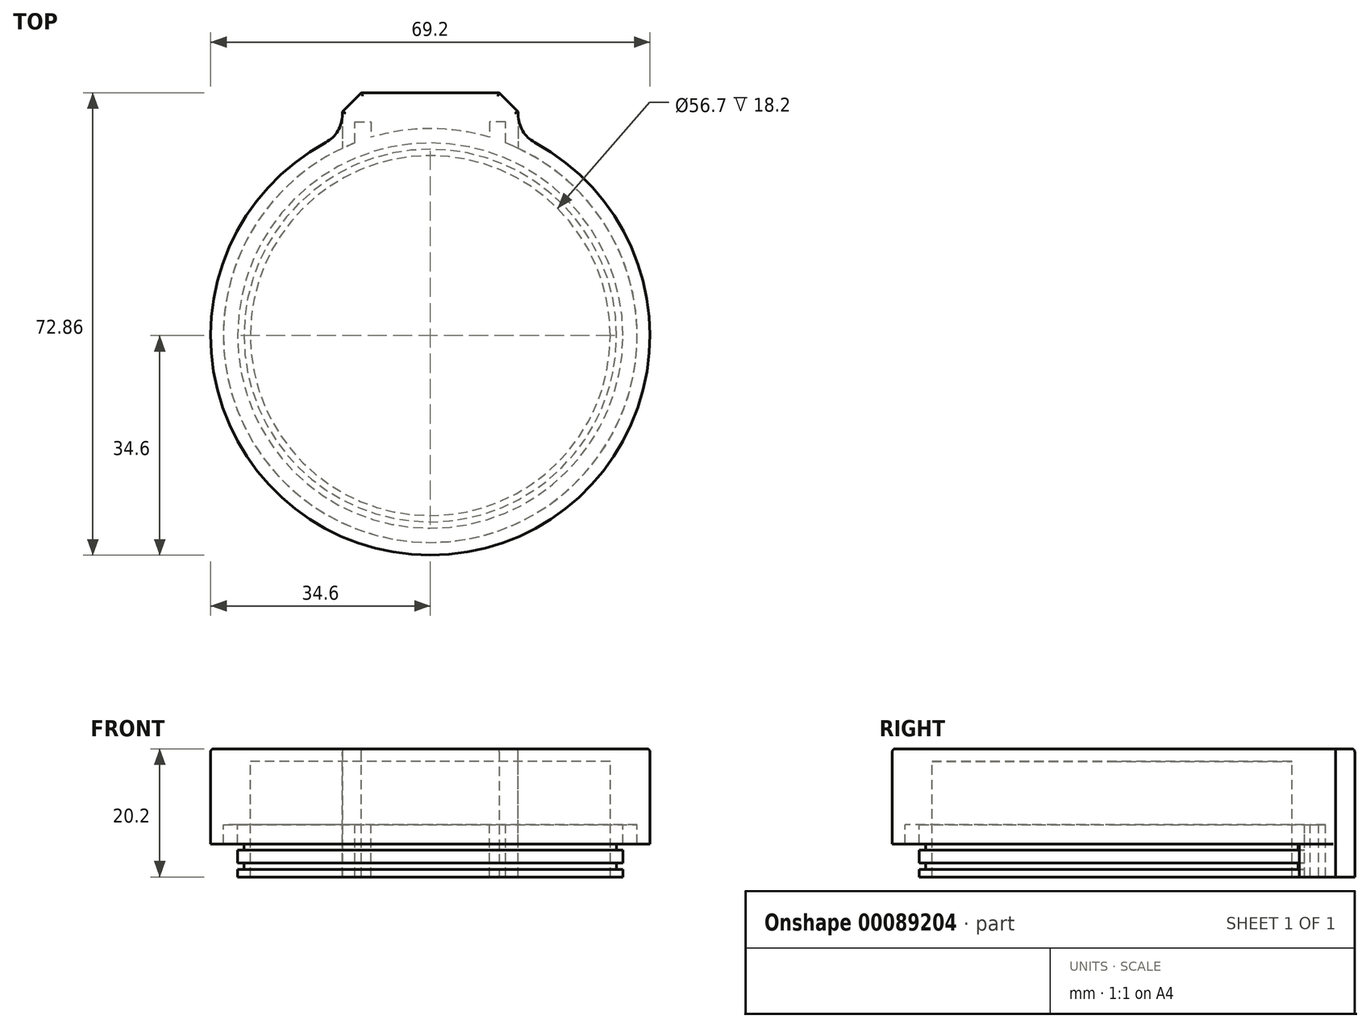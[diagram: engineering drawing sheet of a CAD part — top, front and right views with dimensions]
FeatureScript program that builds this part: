
annotation { "Feature Type Name" : "Feature", "Feature Type Description" : "" }
export const myFeature = defineFeature(function(context is Context, id is Id, definition is map)
    precondition{}
    {
        {
            var Q0;
            Q0=qCreatedBy(makeId("Front.planeOp"),FACE);
            var sketch = newSketch(context, id + "F0", { "sketchPlane" : qUnion([Q0])});
            skLineSegment(sketch, "E0", {"start": v(-30.35, 0) * mm, "end": v(-30.35, 1.2) * mm});
            skLineSegment(sketch, "E1", {"start": v(-30.35, 20.2) * mm, "end": v(0, 20.2) * mm});
            skLineSegment(sketch, "E2", {"start": v(0, 20.2) * mm, "end": v(0, 18.2) * mm});
            skLineSegment(sketch, "E3", {"start": v(0, 18.2) * mm, "end": v(-28.35, 18.2) * mm});
            skLineSegment(sketch, "E4", {"start": v(-30.35, 0) * mm, "end": v(-28.35, 0) * mm});
            skLineSegment(sketch, "E5", {"start": v(-28.35, 0) * mm, "end": v(-28.35, 18.2) * mm});
            skLineSegment(sketch, "E6", {"start": v(-30.35, 2.2) * mm, "end": v(-29.35, 2.2) * mm});
            skLineSegment(sketch, "E7", {"start": v(-29.35, 2.2) * mm, "end": v(-29.35, 1.2) * mm});
            skLineSegment(sketch, "E8", {"start": v(-29.35, 1.2) * mm, "end": v(-30.35, 1.2) * mm});
            skLineSegment(sketch, "E9", {"start": v(-30.35, 5.2) * mm, "end": v(-29.35, 5.2) * mm});
            skLineSegment(sketch, "E10", {"start": v(-29.35, 5.2) * mm, "end": v(-29.35, 4.2) * mm});
            skLineSegment(sketch, "E11", {"start": v(-29.35, 4.2) * mm, "end": v(-30.35, 4.2) * mm});
            skLineSegment(sketch, "E12.trimOffspring", {"start": v(-30.35, 5.2) * mm, "end": v(-30.35, 8.2) * mm});
            skLineSegment(sketch, "E13.trimOffspring", {"start": v(-30.35, 2.2) * mm, "end": v(-30.35, 4.2) * mm});
            skPoint(sketch, "E14.end.orphan", {"position": v(-26, 20.2) * mm});
            skLineSegment(sketch, "E15", {"start": v(-30.35, 20.2) * mm, "end": v(-32.6, 20.2) * mm});
            skPoint(sketch, "E16.end.orphan", {"position": v(-32.55, 18.2) * mm});
            skLineSegment(sketch, "E17", {"start": v(-32.6, 20.2) * mm, "end": v(-32.6, 8.2) * mm});
            skLineSegment(sketch, "E18", {"start": v(-32.6, 8.2) * mm, "end": v(-30.35, 8.2) * mm});
            skPoint(sketch, "E19.orphan", {"position": v(-30.35, 18.2) * mm});
            skSolve(sketch);
        }
        {
            var Q0;
            Q0 = qSketchRegion(id + "F0", true);
            var Q1;
            Q1=sQuery(id+"F0.wireOp",EDGE,"E2");
            revolve(context, id + "F1", {"entities" : qUnion([Q0]), "axis" : qUnion([Q1]), "revolveType" : RevolveType.FULL});
        }
        {
            var Q0;
            Q0=makeQuery(id+"F1.opRevolve","SWEPT_FACE",FACE,{"disambiguationData":[OSD([sQuery(id+"F0.wireOp",EDGE,"E1")])]});
            var sketch = newSketch(context, id + "F2", { "sketchPlane" : qUnion([Q0])});
            skArc(sketch, "E20", {"start": v(-11.85, 30.37) * mm, "mid": v(0, -32.6) * mm, "end": v(11.85, 30.37) * mm});
            skArc(sketch, "E21", {"start": v(-13.85, 31.7) * mm, "mid": v(0, -34.6) * mm, "end": v(13.85, 31.7) * mm});
            skLineSegment(sketch, "E22", {"start": v(-11.85, 30.37) * mm, "end": v(-11.85, 33.67) * mm});
            skLineSegment(sketch, "E23", {"start": v(-11.85, 33.67) * mm, "end": v(-9.35, 33.67) * mm});
            skLineSegment(sketch, "E24", {"start": v(-9.35, 33.67) * mm, "end": v(-9.35, 31.23) * mm});
            skLineSegment(sketch, "E25.MirrorCS", {"start": v(11.85, 33.67) * mm, "end": v(9.35, 33.67) * mm});
            skLineSegment(sketch, "E26.MirrorCS", {"start": v(9.35, 33.67) * mm, "end": v(9.35, 31.23) * mm});
            skLineSegment(sketch, "E27.MirrorCS", {"start": v(11.85, 30.37) * mm, "end": v(11.85, 33.67) * mm});
            skArc(sketch, "E28.trimOffspring", {"start": v(9.35, 31.23) * mm, "mid": v(0, 32.6) * mm, "end": v(-9.35, 31.23) * mm, "construction": true});
            skLineSegment(sketch, "E29", {"start": v(-13.85, 31.7) * mm, "end": v(-13.85, 38.26) * mm});
            skLineSegment(sketch, "E30", {"start": v(-13.85, 38.26) * mm, "end": v(13.85, 38.26) * mm});
            skLineSegment(sketch, "E31", {"start": v(13.85, 38.26) * mm, "end": v(13.85, 31.7) * mm});
            skArc(sketch, "E32.trimOffspring", {"start": v(9.35, 31.23) * mm, "mid": v(0, 32.6) * mm, "end": v(-9.35, 31.23) * mm});
            skSolve(sketch);
        }
        {
            var Q0;
            Q0 = qSketchRegion(id + "F2", true);
            extrude(context, id + "F3", {"entities" : qUnion([Q0]), "operationType" : NewBodyOperationType.ADD, "oppositeDirection" : true, "depth" : 15 * mm});
        }
        {
            var Q0;
            Q0=makeQuery(id+"F1.opRevolve","SWEPT_FACE",FACE,{"disambiguationData":[OSD([sQuery(id+"F0.wireOp",EDGE,"E18")])]});
            var sketch = newSketch(context, id + "F4", { "sketchPlane" : qUnion([Q0])});
            skArc(sketch, "E33.0", {"start": v(-13.85, -31.7) * mm, "mid": v(0, 34.6) * mm, "end": v(13.85, -31.7) * mm});
            skLineSegment(sketch, "E33.1", {"start": v(-13.85, -31.7) * mm, "end": v(-13.85, -38.26) * mm});
            skLineSegment(sketch, "E33.2", {"start": v(-13.85, -38.26) * mm, "end": v(13.85, -38.26) * mm});
            skLineSegment(sketch, "E33.3", {"start": v(13.85, -38.26) * mm, "end": v(13.85, -31.7) * mm});
            skCircle(sketch, "E33.4", {"center": v(0, 0) * mm, "radius": 30.35 * mm});
            skSolve(sketch);
        }
        {
            var Q0;
            Q0 = qSketchRegion(id + "F4", true);
            extrude(context, id + "F5", {"entities" : qUnion([Q0]), "operationType" : NewBodyOperationType.ADD, "oppositeDirection" : true, "depth" : 12 * mm});
        }
        {
            var Q0;
            Q0=makeQuery(id+"F1.opRevolve","SWEPT_FACE",FACE,{"disambiguationData":[OSD([sQuery(id+"F0.wireOp",EDGE,"E3")])]});
            var sketch = newSketch(context, id + "F6", { "sketchPlane" : qUnion([Q0])});
            skSolve(sketch);
        }
        {
            var Q0;
            Q0=makeQuery(id+"F3.opExtrude","CAP_FACE",FACE,{"disambiguationData":[OSD([sQuery(id+"F2.wireOp",EDGE,"E21"),sQuery(id+"F2.wireOp",EDGE,"E22"),sQuery(id+"F2.wireOp",EDGE,"E23"),sQuery(id+"F2.wireOp",EDGE,"E24"),sQuery(id+"F2.wireOp",EDGE,"E25.MirrorCS"),sQuery(id+"F2.wireOp",EDGE,"E26.MirrorCS"),sQuery(id+"F2.wireOp",EDGE,"E27.MirrorCS"),sQuery(id+"F2.wireOp",EDGE,"E29"),sQuery(id+"F2.wireOp",EDGE,"E30"),sQuery(id+"F2.wireOp",EDGE,"E31"),sQuery(id+"F2.wireOp",EDGE,"E20"),sQuery(id+"F2.wireOp",EDGE,"E32.trimOffspring")])],"isStart":false});
            var sketch = newSketch(context, id + "F7", { "sketchPlane" : qUnion([Q0])});
            skLineSegment(sketch, "E34", {"start": v(-13.85, -38.26) * mm, "end": v(13.85, -38.26) * mm});
            skLineSegment(sketch, "E35", {"start": v(13.85, -38.26) * mm, "end": v(13.85, -29.51) * mm});
            skLineSegment(sketch, "E36", {"start": v(-13.85, -38.26) * mm, "end": v(-13.85, -29.51) * mm});
            skArc(sketch, "E37.0", {"start": v(-11.85, -30.37) * mm, "mid": v(-12.86, -29.96) * mm, "end": v(-13.85, -29.51) * mm});
            skLineSegment(sketch, "E37.1", {"start": v(-11.85, -30.37) * mm, "end": v(-11.85, -33.67) * mm});
            skLineSegment(sketch, "E37.2", {"start": v(-11.85, -33.67) * mm, "end": v(-9.35, -33.67) * mm});
            skLineSegment(sketch, "E37.3", {"start": v(-9.35, -33.67) * mm, "end": v(-9.35, -31.23) * mm});
            skArc(sketch, "E37.4", {"start": v(9.35, -31.23) * mm, "mid": v(0, -32.6) * mm, "end": v(-9.35, -31.23) * mm});
            skLineSegment(sketch, "E37.5", {"start": v(9.35, -33.67) * mm, "end": v(9.35, -31.23) * mm});
            skLineSegment(sketch, "E37.6", {"start": v(11.85, -33.67) * mm, "end": v(9.35, -33.67) * mm});
            skLineSegment(sketch, "E37.7", {"start": v(11.85, -30.37) * mm, "end": v(11.85, -33.67) * mm});
            skArc(sketch, "E38.trimOffspring", {"start": v(13.85, -29.51) * mm, "mid": v(12.86, -29.96) * mm, "end": v(11.85, -30.37) * mm});
            skSolve(sketch);
        }
        {
            var Q0;
            Q0 = qSketchRegion(id + "F7", true);
            var Q1;
            Q1=makeQuery(id+"F1.opRevolve","SWEPT_FACE",FACE,{"disambiguationData":[OSD([sQuery(id+"F0.wireOp",EDGE,"E4")])]});
            extrude(context, id + "F8", {"entities" : qUnion([Q0]), "operationType" : NewBodyOperationType.ADD, "endBound" : BoundingType.UP_TO_SURFACE, "endBoundEntityFace" : qUnion([Q1]), "depth" : 25 * mm});
        }
        {
            var Q0;
            Q0=makeQuery(id+"F3.opExtrude","SWEPT_EDGE",EDGE,{"disambiguationData":[OSD([sQuery(id+"F2.wireOp",EDGE,"E21"),sQuery(id+"F2.wireOp",EDGE,"E29")])]});
            var Q1;
            Q1=makeQuery(id+"F3.opExtrude","SWEPT_EDGE",EDGE,{"disambiguationData":[OSD([sQuery(id+"F2.wireOp",EDGE,"E21"),sQuery(id+"F2.wireOp",EDGE,"E31")])]});
            var Q2;
            Q2=makeQuery(id+"F8.opExtrude","CAP_EDGE",EDGE,{"disambiguationData":[OSD([sQuery(id+"F7.wireOp",EDGE,"E36")])],"isStart":true});
            var Q3;
            Q3=makeQuery(id+"F8.opExtrude","CAP_EDGE",EDGE,{"disambiguationData":[OSD([sQuery(id+"F7.wireOp",EDGE,"E35")])],"isStart":true});
            fillet(context, id + "F9", {"entities" : qUnion([Q0, Q1, Q2, Q3]), "radius" : 5 * mm, "tangentPropagation" : true, "allowEdgeOverflow" : false});
        }
        {
            var Q0;
            Q0=makeQuery(id+"F8.boolean.opBoolean","MERGE",EDGE,{"derivedFrom":[makeQuery(id+"F3.opExtrude","SWEPT_EDGE",EDGE,{"disambiguationData":[OSD([sQuery(id+"F2.wireOp",EDGE,"E30"),sQuery(id+"F2.wireOp",EDGE,"E31")])]}),makeQuery(id+"F8.opExtrude","SWEPT_EDGE",EDGE,{"disambiguationData":[OSD([sQuery(id+"F7.wireOp",EDGE,"E34"),sQuery(id+"F7.wireOp",EDGE,"E35")])]})]});
            var Q1;
            Q1=makeQuery(id+"F8.boolean.opBoolean","MERGE",EDGE,{"derivedFrom":[makeQuery(id+"F3.opExtrude","SWEPT_EDGE",EDGE,{"disambiguationData":[OSD([sQuery(id+"F2.wireOp",EDGE,"E29"),sQuery(id+"F2.wireOp",EDGE,"E30")])]}),makeQuery(id+"F8.opExtrude","SWEPT_EDGE",EDGE,{"disambiguationData":[OSD([sQuery(id+"F7.wireOp",EDGE,"E34"),sQuery(id+"F7.wireOp",EDGE,"E36")])]})]});
            chamfer(context, id + "F10", {"entities" : qUnion([Q0, Q1]), "width" : 3 * mm, "tangentPropagation" : true});
        }
        {
            var Q0;
            Q0=makeQuery(id+"F3.opExtrude","CAP_EDGE",EDGE,{"disambiguationData":[OSD([sQuery(id+"F2.wireOp",EDGE,"E30")])],"isStart":true});
            var Q1;
            {var subQ0=sQuery(id+"F2.wireOp",EDGE,"E30");var subQ1=sQuery(id+"F2.wireOp",EDGE,"E29");Q1=makeQuery(id+"F10.opChamfer","BLEND_EDGE",EDGE,{"blendedFrom":[makeQuery(id+"F8.boolean.opBoolean","MERGE",EDGE,{"derivedFrom":[makeQuery(id+"F3.opExtrude","SWEPT_EDGE",EDGE,{"disambiguationData":[OSD([subQ1,subQ0])]}),makeQuery(id+"F8.opExtrude","SWEPT_EDGE",EDGE,{"disambiguationData":[OSD([sQuery(id+"F7.wireOp",EDGE,"E34"),sQuery(id+"F7.wireOp",EDGE,"E36")])]})]}),makeQuery(id+"F5.boolean.opBoolean","MERGE",FACE,{"derivedFrom":[makeQuery(id+"F3.boolean.opBoolean","MERGE",FACE,{"derivedFrom":[makeQuery(id+"F1.opRevolve","SWEPT_FACE",FACE,{"disambiguationData":[OSD([sQuery(id+"F0.wireOp",EDGE,"E1"),sQuery(id+"F0.wireOp",EDGE,"E15")])]}),makeQuery(id+"F3.opExtrude","CAP_FACE",FACE,{"disambiguationData":[OSD([sQuery(id+"F2.wireOp",EDGE,"E21"),sQuery(id+"F2.wireOp",EDGE,"E22"),sQuery(id+"F2.wireOp",EDGE,"E23"),sQuery(id+"F2.wireOp",EDGE,"E24"),sQuery(id+"F2.wireOp",EDGE,"E25.MirrorCS"),sQuery(id+"F2.wireOp",EDGE,"E26.MirrorCS"),sQuery(id+"F2.wireOp",EDGE,"E27.MirrorCS"),subQ1,subQ0,sQuery(id+"F2.wireOp",EDGE,"E31"),sQuery(id+"F2.wireOp",EDGE,"E20"),sQuery(id+"F2.wireOp",EDGE,"E32.trimOffspring")])],"isStart":true})]}),makeQuery(id+"F5.opExtrude","CAP_FACE",FACE,{"disambiguationData":[OSD([sQuery(id+"F4.wireOp",EDGE,"E33.0"),sQuery(id+"F4.wireOp",EDGE,"E33.1"),sQuery(id+"F4.wireOp",EDGE,"E33.2"),sQuery(id+"F4.wireOp",EDGE,"E33.3"),sQuery(id+"F4.wireOp",EDGE,"E33.4")])],"isStart":false})]})],"blendedInto":[makeQuery(id+"F5.boolean.opBoolean","MERGE",FACE,{"derivedFrom":[makeQuery(id+"F3.boolean.opBoolean","MERGE",FACE,{"derivedFrom":[makeQuery(id+"F1.opRevolve","SWEPT_FACE",FACE,{"disambiguationData":[OSD([sQuery(id+"F0.wireOp",EDGE,"E1"),sQuery(id+"F0.wireOp",EDGE,"E15")])]}),makeQuery(id+"F3.opExtrude","CAP_FACE",FACE,{"disambiguationData":[OSD([sQuery(id+"F2.wireOp",EDGE,"E21"),sQuery(id+"F2.wireOp",EDGE,"E22"),sQuery(id+"F2.wireOp",EDGE,"E23"),sQuery(id+"F2.wireOp",EDGE,"E24"),sQuery(id+"F2.wireOp",EDGE,"E25.MirrorCS"),sQuery(id+"F2.wireOp",EDGE,"E26.MirrorCS"),sQuery(id+"F2.wireOp",EDGE,"E27.MirrorCS"),subQ1,subQ0,sQuery(id+"F2.wireOp",EDGE,"E31"),sQuery(id+"F2.wireOp",EDGE,"E20"),sQuery(id+"F2.wireOp",EDGE,"E32.trimOffspring")])],"isStart":true})]}),makeQuery(id+"F5.opExtrude","CAP_FACE",FACE,{"disambiguationData":[OSD([sQuery(id+"F4.wireOp",EDGE,"E33.0"),sQuery(id+"F4.wireOp",EDGE,"E33.1"),sQuery(id+"F4.wireOp",EDGE,"E33.2"),sQuery(id+"F4.wireOp",EDGE,"E33.3"),sQuery(id+"F4.wireOp",EDGE,"E33.4")])],"isStart":false})]})]});}
            var Q2;
            Q2=makeQuery(id+"F3.opExtrude","CAP_EDGE",EDGE,{"disambiguationData":[OSD([sQuery(id+"F2.wireOp",EDGE,"E21")])],"isStart":true});
            var Q3;
            {var subQ0=sQuery(id+"F2.wireOp",EDGE,"E31");var subQ1=sQuery(id+"F2.wireOp",EDGE,"E30");Q3=makeQuery(id+"F10.opChamfer","BLEND_EDGE",EDGE,{"blendedFrom":[makeQuery(id+"F8.boolean.opBoolean","MERGE",EDGE,{"derivedFrom":[makeQuery(id+"F3.opExtrude","SWEPT_EDGE",EDGE,{"disambiguationData":[OSD([subQ1,subQ0])]}),makeQuery(id+"F8.opExtrude","SWEPT_EDGE",EDGE,{"disambiguationData":[OSD([sQuery(id+"F7.wireOp",EDGE,"E34"),sQuery(id+"F7.wireOp",EDGE,"E35")])]})]}),makeQuery(id+"F5.boolean.opBoolean","MERGE",FACE,{"derivedFrom":[makeQuery(id+"F3.boolean.opBoolean","MERGE",FACE,{"derivedFrom":[makeQuery(id+"F1.opRevolve","SWEPT_FACE",FACE,{"disambiguationData":[OSD([sQuery(id+"F0.wireOp",EDGE,"E1"),sQuery(id+"F0.wireOp",EDGE,"E15")])]}),makeQuery(id+"F3.opExtrude","CAP_FACE",FACE,{"disambiguationData":[OSD([sQuery(id+"F2.wireOp",EDGE,"E21"),sQuery(id+"F2.wireOp",EDGE,"E22"),sQuery(id+"F2.wireOp",EDGE,"E23"),sQuery(id+"F2.wireOp",EDGE,"E24"),sQuery(id+"F2.wireOp",EDGE,"E25.MirrorCS"),sQuery(id+"F2.wireOp",EDGE,"E26.MirrorCS"),sQuery(id+"F2.wireOp",EDGE,"E27.MirrorCS"),sQuery(id+"F2.wireOp",EDGE,"E29"),subQ1,subQ0,sQuery(id+"F2.wireOp",EDGE,"E20"),sQuery(id+"F2.wireOp",EDGE,"E32.trimOffspring")])],"isStart":true})]}),makeQuery(id+"F5.opExtrude","CAP_FACE",FACE,{"disambiguationData":[OSD([sQuery(id+"F4.wireOp",EDGE,"E33.0"),sQuery(id+"F4.wireOp",EDGE,"E33.1"),sQuery(id+"F4.wireOp",EDGE,"E33.2"),sQuery(id+"F4.wireOp",EDGE,"E33.3"),sQuery(id+"F4.wireOp",EDGE,"E33.4")])],"isStart":false})]})],"blendedInto":[makeQuery(id+"F5.boolean.opBoolean","MERGE",FACE,{"derivedFrom":[makeQuery(id+"F3.boolean.opBoolean","MERGE",FACE,{"derivedFrom":[makeQuery(id+"F1.opRevolve","SWEPT_FACE",FACE,{"disambiguationData":[OSD([sQuery(id+"F0.wireOp",EDGE,"E1"),sQuery(id+"F0.wireOp",EDGE,"E15")])]}),makeQuery(id+"F3.opExtrude","CAP_FACE",FACE,{"disambiguationData":[OSD([sQuery(id+"F2.wireOp",EDGE,"E21"),sQuery(id+"F2.wireOp",EDGE,"E22"),sQuery(id+"F2.wireOp",EDGE,"E23"),sQuery(id+"F2.wireOp",EDGE,"E24"),sQuery(id+"F2.wireOp",EDGE,"E25.MirrorCS"),sQuery(id+"F2.wireOp",EDGE,"E26.MirrorCS"),sQuery(id+"F2.wireOp",EDGE,"E27.MirrorCS"),sQuery(id+"F2.wireOp",EDGE,"E29"),subQ1,subQ0,sQuery(id+"F2.wireOp",EDGE,"E20"),sQuery(id+"F2.wireOp",EDGE,"E32.trimOffspring")])],"isStart":true})]}),makeQuery(id+"F5.opExtrude","CAP_FACE",FACE,{"disambiguationData":[OSD([sQuery(id+"F4.wireOp",EDGE,"E33.0"),sQuery(id+"F4.wireOp",EDGE,"E33.1"),sQuery(id+"F4.wireOp",EDGE,"E33.2"),sQuery(id+"F4.wireOp",EDGE,"E33.3"),sQuery(id+"F4.wireOp",EDGE,"E33.4")])],"isStart":false})]})]});}
            var Q4;
            {var subQ0=sQuery(id+"F2.wireOp",EDGE,"E29");var subQ1=sQuery(id+"F2.wireOp",EDGE,"E21");Q4=makeQuery(id+"F9.opFillet","BLEND_EDGE",EDGE,{"blendedFrom":[makeQuery(id+"F3.opExtrude","SWEPT_EDGE",EDGE,{"disambiguationData":[OSD([subQ1,subQ0])]}),makeQuery(id+"F5.boolean.opBoolean","MERGE",FACE,{"derivedFrom":[makeQuery(id+"F3.boolean.opBoolean","MERGE",FACE,{"derivedFrom":[makeQuery(id+"F1.opRevolve","SWEPT_FACE",FACE,{"disambiguationData":[OSD([sQuery(id+"F0.wireOp",EDGE,"E1"),sQuery(id+"F0.wireOp",EDGE,"E15")])]}),makeQuery(id+"F3.opExtrude","CAP_FACE",FACE,{"disambiguationData":[OSD([subQ1,sQuery(id+"F2.wireOp",EDGE,"E22"),sQuery(id+"F2.wireOp",EDGE,"E23"),sQuery(id+"F2.wireOp",EDGE,"E24"),sQuery(id+"F2.wireOp",EDGE,"E25.MirrorCS"),sQuery(id+"F2.wireOp",EDGE,"E26.MirrorCS"),sQuery(id+"F2.wireOp",EDGE,"E27.MirrorCS"),subQ0,sQuery(id+"F2.wireOp",EDGE,"E30"),sQuery(id+"F2.wireOp",EDGE,"E31"),sQuery(id+"F2.wireOp",EDGE,"E20"),sQuery(id+"F2.wireOp",EDGE,"E32.trimOffspring")])],"isStart":true})]}),makeQuery(id+"F5.opExtrude","CAP_FACE",FACE,{"disambiguationData":[OSD([sQuery(id+"F4.wireOp",EDGE,"E33.0"),sQuery(id+"F4.wireOp",EDGE,"E33.1"),sQuery(id+"F4.wireOp",EDGE,"E33.2"),sQuery(id+"F4.wireOp",EDGE,"E33.3"),sQuery(id+"F4.wireOp",EDGE,"E33.4")])],"isStart":false})]})],"blendedInto":[makeQuery(id+"F5.boolean.opBoolean","MERGE",FACE,{"derivedFrom":[makeQuery(id+"F3.boolean.opBoolean","MERGE",FACE,{"derivedFrom":[makeQuery(id+"F1.opRevolve","SWEPT_FACE",FACE,{"disambiguationData":[OSD([sQuery(id+"F0.wireOp",EDGE,"E1"),sQuery(id+"F0.wireOp",EDGE,"E15")])]}),makeQuery(id+"F3.opExtrude","CAP_FACE",FACE,{"disambiguationData":[OSD([subQ1,sQuery(id+"F2.wireOp",EDGE,"E22"),sQuery(id+"F2.wireOp",EDGE,"E23"),sQuery(id+"F2.wireOp",EDGE,"E24"),sQuery(id+"F2.wireOp",EDGE,"E25.MirrorCS"),sQuery(id+"F2.wireOp",EDGE,"E26.MirrorCS"),sQuery(id+"F2.wireOp",EDGE,"E27.MirrorCS"),subQ0,sQuery(id+"F2.wireOp",EDGE,"E30"),sQuery(id+"F2.wireOp",EDGE,"E31"),sQuery(id+"F2.wireOp",EDGE,"E20"),sQuery(id+"F2.wireOp",EDGE,"E32.trimOffspring")])],"isStart":true})]}),makeQuery(id+"F5.opExtrude","CAP_FACE",FACE,{"disambiguationData":[OSD([sQuery(id+"F4.wireOp",EDGE,"E33.0"),sQuery(id+"F4.wireOp",EDGE,"E33.1"),sQuery(id+"F4.wireOp",EDGE,"E33.2"),sQuery(id+"F4.wireOp",EDGE,"E33.3"),sQuery(id+"F4.wireOp",EDGE,"E33.4")])],"isStart":false})]})]});}
            var Q5;
            Q5=makeQuery(id+"F3.opExtrude","CAP_EDGE",EDGE,{"disambiguationData":[OSD([sQuery(id+"F2.wireOp",EDGE,"E29")])],"isStart":true});
            fillet(context, id + "F11", {"entities" : qUnion([Q0, Q1, Q2, Q3, Q4, Q5]), "radius" : 0.5 * mm, "tangentPropagation" : true, "allowEdgeOverflow" : false});
        }
    });
